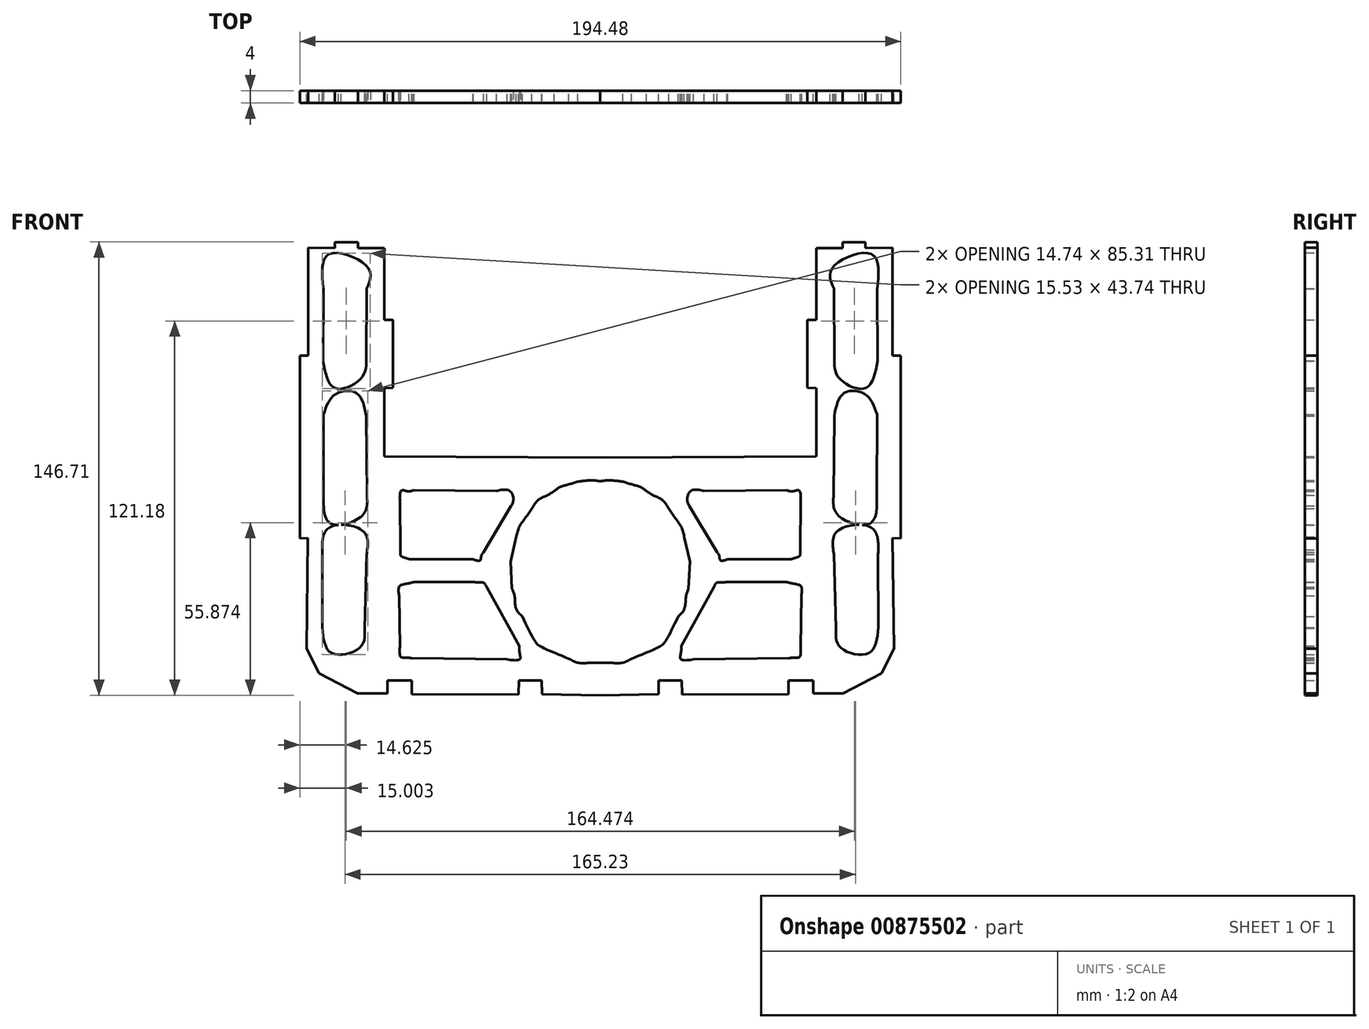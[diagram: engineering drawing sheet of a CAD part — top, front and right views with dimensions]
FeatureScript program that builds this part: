
annotation { "Feature Type Name" : "Feature", "Feature Type Description" : "" }
export const myFeature = defineFeature(function(context is Context, id is Id, definition is map)
    precondition{}
    {
        {
            var Q0;
            Q0=qCreatedBy(makeId("Front.planeOp"),FACE);
            var sketch = newSketch(context, id + "F0", { "sketchPlane" : qUnion([Q0])});
            skLineSegment(sketch, "E0", {"start": v(89.64, 58.45) * mm, "end": v(89.75, 35.15) * mm});
            skLineSegment(sketch, "E1", {"start": v(75.72, 35.27) * mm, "end": v(75.65, 58.52) * mm});
            skLineSegment(sketch, "E2", {"start": v(0, -73.07) * mm, "end": v(18.86, -72.7) * mm});
            skLineSegment(sketch, "E3", {"start": v(18.86, -72.7) * mm, "end": v(18.93, -68.35) * mm});
            skLineSegment(sketch, "E4", {"start": v(18.93, -68.35) * mm, "end": v(26.4, -68.3) * mm});
            skLineSegment(sketch, "E5", {"start": v(26.4, -68.3) * mm, "end": v(26.45, -72.85) * mm});
            skLineSegment(sketch, "E6", {"start": v(26.45, -72.85) * mm, "end": v(60.95, -72.78) * mm});
            skLineSegment(sketch, "E7", {"start": v(60.95, -72.78) * mm, "end": v(60.95, -68.25) * mm});
            skLineSegment(sketch, "E8", {"start": v(60.95, -68.25) * mm, "end": v(68.89, -68.25) * mm});
            skLineSegment(sketch, "E9", {"start": v(68.89, -68.25) * mm, "end": v(68.89, -72.5) * mm});
            skLineSegment(sketch, "E10", {"start": v(68.89, -72.5) * mm, "end": v(78.52, -72.5) * mm});
            skLineSegment(sketch, "E11", {"start": v(78.52, -72.5) * mm, "end": v(91, -65.98) * mm});
            skLineSegment(sketch, "E12", {"start": v(91, -65.98) * mm, "end": v(95.04, -58.04) * mm});
            skLineSegment(sketch, "E13", {"start": v(95.04, -58.04) * mm, "end": v(94.64, -22.19) * mm});
            skLineSegment(sketch, "E14", {"start": v(94.64, -22.19) * mm, "end": v(97.24, -22.29) * mm});
            skLineSegment(sketch, "E15", {"start": v(97.24, -22.29) * mm, "end": v(97.23, 36.93) * mm});
            skLineSegment(sketch, "E16", {"start": v(97.23, 36.93) * mm, "end": v(94.54, 36.93) * mm});
            skLineSegment(sketch, "E17", {"start": v(94.54, 36.93) * mm, "end": v(94.54, 71.8) * mm});
            skLineSegment(sketch, "E18", {"start": v(94.54, 71.8) * mm, "end": v(85.84, 71.73) * mm});
            skLineSegment(sketch, "E19", {"start": v(85.84, 71.73) * mm, "end": v(85.84, 73.63) * mm});
            skLineSegment(sketch, "E20", {"start": v(85.84, 73.63) * mm, "end": v(78.38, 73.64) * mm});
            skLineSegment(sketch, "E21", {"start": v(78.38, 73.64) * mm, "end": v(78.4, 71.63) * mm});
            skLineSegment(sketch, "E22", {"start": v(78.4, 71.63) * mm, "end": v(69.88, 71.65) * mm});
            skLineSegment(sketch, "E23", {"start": v(69.88, 71.65) * mm, "end": v(69.88, 48.4) * mm});
            skLineSegment(sketch, "E24", {"start": v(69.88, 48.4) * mm, "end": v(67.04, 48.48) * mm});
            skLineSegment(sketch, "E25", {"start": v(67.04, 48.48) * mm, "end": v(67.04, 26.44) * mm});
            skLineSegment(sketch, "E26", {"start": v(67.04, 26.44) * mm, "end": v(69.95, 26.3) * mm});
            skLineSegment(sketch, "E27", {"start": v(69.95, 26.3) * mm, "end": v(69.95, 4.25) * mm});
            skLineSegment(sketch, "E28", {"start": v(69.95, 4.25) * mm, "end": v(0, 3.88) * mm});
            skLineSegment(sketch, "E29", {"start": v(27.17, -21.79) * mm, "end": v(28.98, -29.86) * mm});
            skLineSegment(sketch, "E30", {"start": v(28.98, -29.86) * mm, "end": v(28.59, -38.62) * mm});
            skLineSegment(sketch, "E31", {"start": v(0.08, -62.58) * mm, "end": v(0.08, -62.58) * mm});
            skLineSegment(sketch, "E32", {"start": v(33.6, -6.95) * mm, "end": v(60.46, -6.75) * mm});
            skLineSegment(sketch, "E33", {"start": v(64.87, -10.16) * mm, "end": v(64.67, -26) * mm});
            skLineSegment(sketch, "E34", {"start": v(61.86, -29) * mm, "end": v(41.22, -29) * mm});
            skLineSegment(sketch, "E35", {"start": v(37.8, -26.8) * mm, "end": v(28.84, -11.76) * mm});
            skLineSegment(sketch, "E36", {"start": v(41.01, -36.42) * mm, "end": v(60.26, -36.42) * mm});
            skLineSegment(sketch, "E37", {"start": v(65.07, -40.83) * mm, "end": v(64.87, -57.47) * mm});
            skLineSegment(sketch, "E38", {"start": v(61.06, -61.07) * mm, "end": v(30.2, -61.48) * mm});
            skLineSegment(sketch, "E39", {"start": v(26.18, -57.07) * mm, "end": v(36.8, -38.02) * mm});
            skLineSegment(sketch, "E40", {"start": v(89.93, -27.4) * mm, "end": v(89.97, -51.16) * mm});
            skLineSegment(sketch, "E41", {"start": v(76.3, -51.45) * mm, "end": v(75.63, -27.54) * mm});
            skLineSegment(sketch, "E42", {"start": v(89.6, 17.78) * mm, "end": v(89.52, -8.36) * mm});
            skLineSegment(sketch, "E43", {"start": v(75.5, -8.36) * mm, "end": v(75.72, 17.35) * mm});
            skFitSpline(sketch, "E44", {"points": [v(75.65, 58.52) * mm, v(75.11, 65.23) * mm, v(87.65, 69.77) * mm, v(89.64, 58.45) * mm]});
            skFitSpline(sketch, "E45", {"points": [v(89.75, 35.15) * mm, v(85.72, 26.3) * mm, v(77.27, 29.67) * mm, v(75.72, 35.27) * mm]});
            skFitSpline(sketch, "E46", {"points": [v(0.12, -3.75) * mm, v(2.53, -3.52) * mm, v(4.93, -3.64) * mm, v(7.34, -3.95) * mm]});
            skFitSpline(sketch, "E47", {"points": [v(7.34, -3.95) * mm, v(10.2, -4.8) * mm, v(13, -5.7) * mm, v(14.96, -6.95) * mm]});
            skFitSpline(sketch, "E48", {"points": [v(14.96, -6.95) * mm, v(17.4, -8.5) * mm, v(19.88, -9.69) * mm, v(22.16, -12.65) * mm]});
            skFitSpline(sketch, "E49", {"points": [v(22.16, -12.65) * mm, v(24.2, -15.63) * mm, v(26.23, -18.62) * mm, v(27.17, -21.79) * mm]});
            skFitSpline(sketch, "E50", {"points": [v(28.59, -38.62) * mm, v(27.7, -41.2) * mm, v(27.3, -44.9) * mm, v(25.18, -47.64) * mm]});
            skFitSpline(sketch, "E51", {"points": [v(25.18, -47.64) * mm, v(20.88, -55.95) * mm, v(18.97, -57.47) * mm, v(10.15, -61.27) * mm]});
            skFitSpline(sketch, "E52", {"points": [v(10.15, -61.27) * mm, v(6.98, -62.58) * mm, v(3.43, -62.57) * mm, v(0.08, -62.58) * mm]});
            skFitSpline(sketch, "E53", {"points": [v(60.46, -6.75) * mm, v(62.27, -7.06) * mm, v(64.32, -6.78) * mm, v(64.87, -10.16) * mm]});
            skFitSpline(sketch, "E54", {"points": [v(64.67, -26) * mm, v(64.55, -27.93) * mm, v(63.29, -28.56) * mm, v(61.86, -29) * mm]});
            skFitSpline(sketch, "E55", {"points": [v(41.22, -29) * mm, v(38.89, -29.46) * mm, v(38.52, -27.96) * mm, v(37.8, -26.8) * mm]});
            skFitSpline(sketch, "E56", {"points": [v(28.84, -11.76) * mm, v(28.12, -9.86) * mm, v(29.34, -6.9) * mm, v(33.6, -6.95) * mm]});
            skFitSpline(sketch, "E57", {"points": [v(60.26, -36.42) * mm, v(62.75, -37) * mm, v(65, -37.83) * mm, v(65.07, -40.83) * mm]});
            skFitSpline(sketch, "E58", {"points": [v(64.87, -57.47) * mm, v(64.46, -60.76) * mm, v(62.76, -60.92) * mm, v(61.06, -61.07) * mm]});
            skFitSpline(sketch, "E59", {"points": [v(30.2, -61.48) * mm, v(26.02, -61.36) * mm, v(26.12, -59.2) * mm, v(26.18, -57.07) * mm]});
            skFitSpline(sketch, "E60", {"points": [v(36.8, -38.02) * mm, v(37.72, -36.63) * mm, v(39.36, -36.51) * mm, v(41.01, -36.42) * mm]});
            skFitSpline(sketch, "E61", {"points": [v(75.63, -27.54) * mm, v(76.7, -20.03) * mm, v(87.8, -18.86) * mm, v(89.93, -27.4) * mm]});
            skFitSpline(sketch, "E62", {"points": [v(89.97, -51.16) * mm, v(86.97, -59.38) * mm, v(77.7, -57.57) * mm, v(76.3, -51.45) * mm]});
            skFitSpline(sketch, "E63", {"points": [v(75.72, 17.35) * mm, v(78.94, 24.73) * mm, v(85.83, 24.27) * mm, v(89.6, 17.78) * mm]});
            skFitSpline(sketch, "E64", {"points": [v(89.52, -8.36) * mm, v(87.23, -17.45) * mm, v(76.99, -14.82) * mm, v(75.5, -8.36) * mm]});
            skLineSegment(sketch, "E65", {"start": v(0.12, -3.75) * mm, "end": v(0, -3.75) * mm});
            skLineSegment(sketch, "E66", {"start": v(0, -3.75) * mm, "end": v(0, 3.88) * mm});
            skLineSegment(sketch, "E67", {"start": v(0.08, -62.58) * mm, "end": v(0, -62.58) * mm});
            skLineSegment(sketch, "E68", {"start": v(0, -62.58) * mm, "end": v(0, -73.07) * mm});
            skSolve(sketch);
        }
        {
            var Q0;
            Q0 = qSketchRegion(id + "F0", true);
            extrude(context, id + "F1", {"entities" : qUnion([Q0]), "depth" : 4 * mm, "offsetDistance" : 25 * mm});
        }
        {
            var Q0;
            Q0=makeQuery(id+"F1.opExtrude","SWEPT_BODY",BODY,{"disambiguationData":[OSD([sQuery(id+"F0.wireOp",EDGE,"E0"),sQuery(id+"F0.wireOp",EDGE,"E1"),sQuery(id+"F0.wireOp",EDGE,"E2"),sQuery(id+"F0.wireOp",EDGE,"E3"),sQuery(id+"F0.wireOp",EDGE,"E4"),sQuery(id+"F0.wireOp",EDGE,"E5"),sQuery(id+"F0.wireOp",EDGE,"E6"),sQuery(id+"F0.wireOp",EDGE,"E7"),sQuery(id+"F0.wireOp",EDGE,"E8"),sQuery(id+"F0.wireOp",EDGE,"E9"),sQuery(id+"F0.wireOp",EDGE,"E10"),sQuery(id+"F0.wireOp",EDGE,"E11"),sQuery(id+"F0.wireOp",EDGE,"E12"),sQuery(id+"F0.wireOp",EDGE,"E13"),sQuery(id+"F0.wireOp",EDGE,"E14"),sQuery(id+"F0.wireOp",EDGE,"E15"),sQuery(id+"F0.wireOp",EDGE,"E16"),sQuery(id+"F0.wireOp",EDGE,"E17"),sQuery(id+"F0.wireOp",EDGE,"E18"),sQuery(id+"F0.wireOp",EDGE,"E19"),sQuery(id+"F0.wireOp",EDGE,"E20"),sQuery(id+"F0.wireOp",EDGE,"E21"),sQuery(id+"F0.wireOp",EDGE,"E22"),sQuery(id+"F0.wireOp",EDGE,"E23"),sQuery(id+"F0.wireOp",EDGE,"E24"),sQuery(id+"F0.wireOp",EDGE,"E25"),sQuery(id+"F0.wireOp",EDGE,"E26"),sQuery(id+"F0.wireOp",EDGE,"E27"),sQuery(id+"F0.wireOp",EDGE,"E28"),sQuery(id+"F0.wireOp",EDGE,"E29"),sQuery(id+"F0.wireOp",EDGE,"E30"),sQuery(id+"F0.wireOp",EDGE,"E32"),sQuery(id+"F0.wireOp",EDGE,"E33"),sQuery(id+"F0.wireOp",EDGE,"E34"),sQuery(id+"F0.wireOp",EDGE,"E35"),sQuery(id+"F0.wireOp",EDGE,"E36"),sQuery(id+"F0.wireOp",EDGE,"E37"),sQuery(id+"F0.wireOp",EDGE,"E38"),sQuery(id+"F0.wireOp",EDGE,"E39"),sQuery(id+"F0.wireOp",EDGE,"E40"),sQuery(id+"F0.wireOp",EDGE,"E41"),sQuery(id+"F0.wireOp",EDGE,"E42"),sQuery(id+"F0.wireOp",EDGE,"E43"),sQuery(id+"F0.wireOp",EDGE,"E44"),sQuery(id+"F0.wireOp",EDGE,"E45"),sQuery(id+"F0.wireOp",EDGE,"E46"),sQuery(id+"F0.wireOp",EDGE,"E47"),sQuery(id+"F0.wireOp",EDGE,"E48"),sQuery(id+"F0.wireOp",EDGE,"E49"),sQuery(id+"F0.wireOp",EDGE,"E50"),sQuery(id+"F0.wireOp",EDGE,"E51"),sQuery(id+"F0.wireOp",EDGE,"E52"),sQuery(id+"F0.wireOp",EDGE,"E53"),sQuery(id+"F0.wireOp",EDGE,"E54"),sQuery(id+"F0.wireOp",EDGE,"E55"),sQuery(id+"F0.wireOp",EDGE,"E56"),sQuery(id+"F0.wireOp",EDGE,"E57"),sQuery(id+"F0.wireOp",EDGE,"E58"),sQuery(id+"F0.wireOp",EDGE,"E59"),sQuery(id+"F0.wireOp",EDGE,"E60"),sQuery(id+"F0.wireOp",EDGE,"E61"),sQuery(id+"F0.wireOp",EDGE,"E62"),sQuery(id+"F0.wireOp",EDGE,"E63"),sQuery(id+"F0.wireOp",EDGE,"E64"),sQuery(id+"F0.wireOp",EDGE,"E65"),sQuery(id+"F0.wireOp",EDGE,"E66"),sQuery(id+"F0.wireOp",EDGE,"E67"),sQuery(id+"F0.wireOp",EDGE,"E68")])]});
            var Q1;
            Q1=qCreatedBy(makeId("Right.planeOp"),FACE);
            mirror(context, id + "F2", {"operationType" : NewBodyOperationType.ADD, "entities" : qUnion([Q0]), "mirrorPlane" : qUnion([Q1])});
        }
    });
